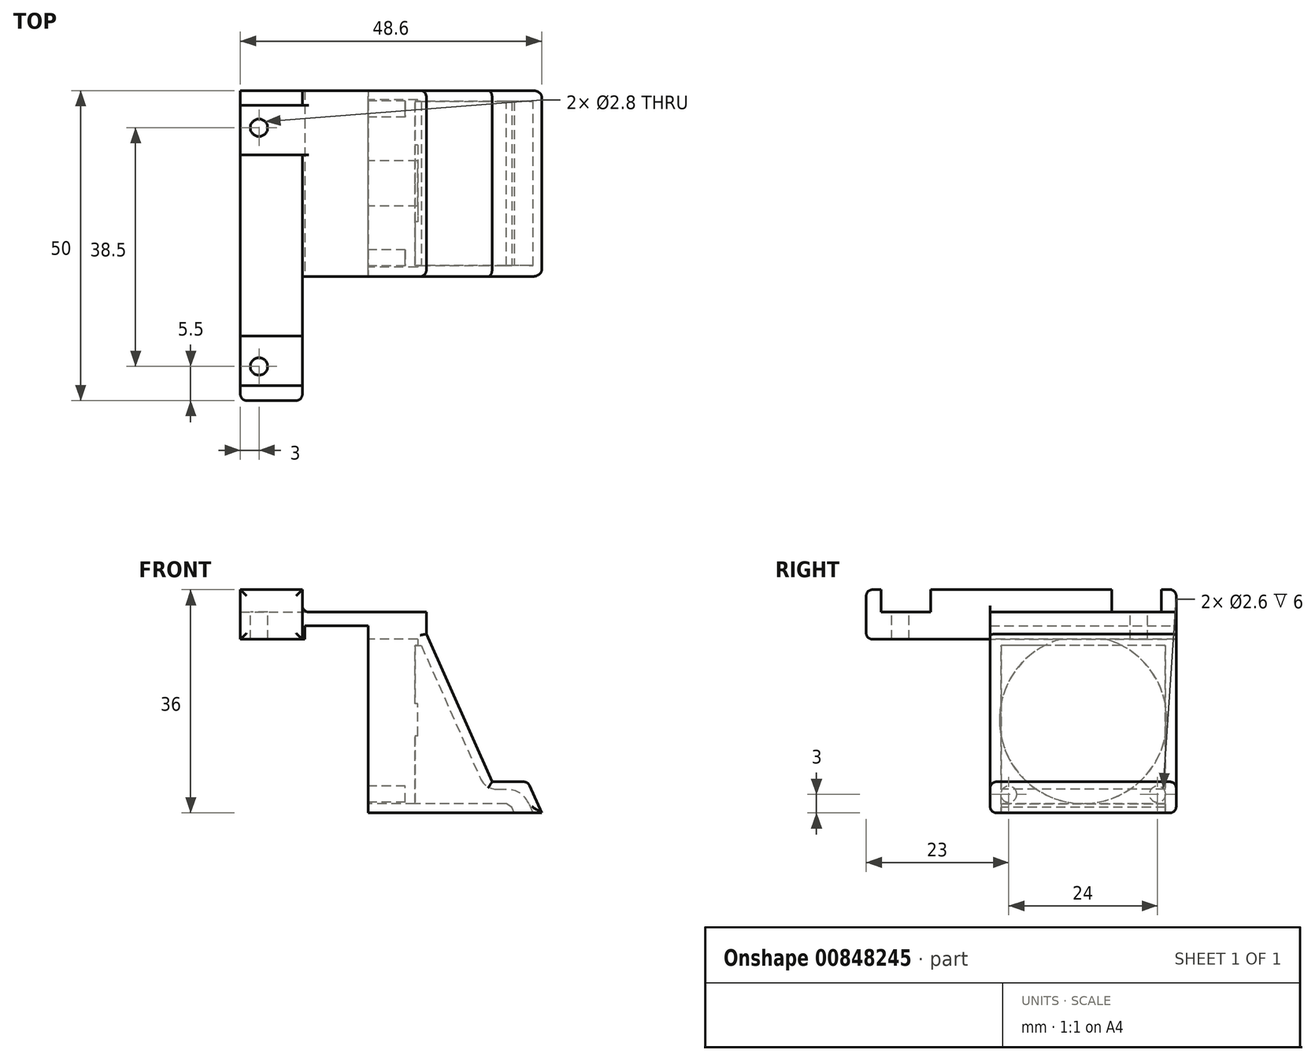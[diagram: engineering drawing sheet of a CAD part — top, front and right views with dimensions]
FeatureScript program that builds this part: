
annotation { "Feature Type Name" : "Feature", "Feature Type Description" : "" }
export const myFeature = defineFeature(function(context is Context, id is Id, definition is map)
    precondition{}
    {
        {
            var Q0;
            Q0=qCreatedBy(makeId("Front.planeOp"),FACE);
            var sketch = newSketch(context, id + "F0", { "sketchPlane" : qUnion([Q0])});
            skLineSegment(sketch, "E0", {"start": v(0, 0) * mm, "end": v(0, 32) * mm});
            skLineSegment(sketch, "E1", {"start": v(0, 32) * mm, "end": v(8, 32) * mm});
            skLineSegment(sketch, "E2", {"start": v(8, 32) * mm, "end": v(20, 5) * mm});
            skLineSegment(sketch, "E3", {"start": v(28, 0) * mm, "end": v(0, 0) * mm});
            skLineSegment(sketch, "E4", {"start": v(20, 5) * mm, "end": v(25.78, 5) * mm});
            skLineSegment(sketch, "E5", {"start": v(25.78, 5) * mm, "end": v(28, 0) * mm});
            skSolve(sketch);
        }
        {
            var Q0;
            Q0=makeQuery(id+"F0.imprint","IMPRINT",FACE,{"disambiguationData":[TD([[makeQuery(id+"F0.imprint","IMPRINT",EDGE,{"derivedFrom":sQuery(id+"F0.wireOp",EDGE,"E0")}),-1.0]])]});
            extrude(context, id + "F1", {"entities" : qUnion([Q0]), "depth" : 30 * mm, "offsetDistance" : 25 * mm});
        }
        {
            var Q0;
            Q0=makeQuery(id+"F1.opExtrude","SWEPT_FACE",FACE,{"disambiguationData":[OSD([sQuery(id+"F0.wireOp",EDGE,"E1")])]});
            var sketch = newSketch(context, id + "F2", { "sketchPlane" : qUnion([Q0])});
            skLineSegment(sketch, "E6.bottom", {"start": v(-20.6, -50) * mm, "end": v(-10.6, -50) * mm});
            skLineSegment(sketch, "E6.top", {"start": v(0, 0) * mm, "end": v(9.4, 0) * mm});
            skLineSegment(sketch, "E6.left", {"start": v(-20.6, -50) * mm, "end": v(-20.6, 0) * mm});
            skLineSegment(sketch, "E6.right", {"start": v(9.4, -30) * mm, "end": v(9.4, 0) * mm});
            skLineSegment(sketch, "E7", {"start": v(9.4, -30) * mm, "end": v(-10.6, -30) * mm});
            skLineSegment(sketch, "E8", {"start": v(-10.6, -30) * mm, "end": v(-10.6, -50) * mm});
            skLineSegment(sketch, "E9", {"start": v(9.4, 0) * mm, "end": v(0, 0) * mm});
            skLineSegment(sketch, "E10", {"start": v(-20.6, 0) * mm, "end": v(0, 0) * mm});
            skSolve(sketch);
        }
        {
            var Q0;
            Q0=qSketchRegion(id+"F2",true);
            extrude(context, id + "F3", {"entities" : qUnion([Q0]), "operationType" : NewBodyOperationType.ADD, "endBound" : BoundingType.SYMMETRIC, "oppositeDirection" : true, "depth" : 8 * mm, "offsetDistance" : 25 * mm});
        }
        {
            var Q0;
            Q0=qCreatedBy(makeId("Top.planeOp"),FACE);
            cPlane(context, id + "F4", {"entities" : qUnion([Q0]), "cplaneType" : CPlaneType.OFFSET, "offset" : 36 * mm, "width" : 150 * mm, "height" : 150 * mm});
        }
        {
            var Q0;
            Q0=qCreatedBy(id+"F4.planeOp",FACE);
            var sketch = newSketch(context, id + "F5", { "sketchPlane" : qUnion([Q0])});
            skLineSegment(sketch, "E11.bottom", {"start": v(-20.6, -39.6) * mm, "end": v(-10.6, -39.6) * mm});
            skLineSegment(sketch, "E11.top", {"start": v(-20.6, -47.6) * mm, "end": v(-10.6, -47.6) * mm});
            skLineSegment(sketch, "E11.left", {"start": v(-20.6, -39.6) * mm, "end": v(-20.6, -47.6) * mm});
            skLineSegment(sketch, "E11.right", {"start": v(-10.6, -39.6) * mm, "end": v(-10.6, -47.6) * mm});
            skLineSegment(sketch, "E12.bottom", {"start": v(-20.6, -2.4) * mm, "end": v(-10.6, -2.4) * mm});
            skLineSegment(sketch, "E12.top", {"start": v(-20.6, -10.4) * mm, "end": v(-10.6, -10.4) * mm});
            skLineSegment(sketch, "E12.left", {"start": v(-20.6, -2.4) * mm, "end": v(-20.6, -10.4) * mm});
            skLineSegment(sketch, "E13", {"start": v(-10.6, -30) * mm, "end": v(-10.6, -10.4) * mm});
            skLineSegment(sketch, "E14", {"start": v(-10.6, -30) * mm, "end": v(9.4, -30) * mm});
            skLineSegment(sketch, "E15", {"start": v(9.4, -30) * mm, "end": v(9.4, 0) * mm});
            skLineSegment(sketch, "E16", {"start": v(9.4, 0) * mm, "end": v(-10.6, 0) * mm});
            skLineSegment(sketch, "E17", {"start": v(-10.6, 0) * mm, "end": v(-10.6, -2.4) * mm});
            skPoint(sketch, "E18.orphan", {"position": v(-8.6, -2.4) * mm});
            skSolve(sketch);
        }
        {
            var Q0;
            Q0=makeQuery(id+"F5.imprint","IMPRINT",FACE,{"disambiguationData":[TD([[makeQuery(id+"F5.imprint","IMPRINT",EDGE,{"derivedFrom":sQuery(id+"F5.wireOp",EDGE,"E11.bottom")}),-1.0]])]});
            var Q1;
            Q1=makeQuery(id+"F5.imprint","IMPRINT",FACE,{"disambiguationData":[TD([[makeQuery(id+"F5.imprint","IMPRINT",EDGE,{"derivedFrom":sQuery(id+"F5.wireOp",EDGE,"E12.bottom")}),-1.0]])]});
            extrude(context, id + "F6", {"entities" : qUnion([Q0, Q1]), "operationType" : NewBodyOperationType.REMOVE, "oppositeDirection" : true, "depth" : 3.6 * mm, "offsetDistance" : 25 * mm});
        }
        {
            var Q0;
            Q0=qCreatedBy(makeId("Front.planeOp"),FACE);
            cPlane(context, id + "F7", {"entities" : qUnion([Q0]), "cplaneType" : CPlaneType.OFFSET, "offset" : 28.25 * mm, "width" : 150 * mm, "height" : 150 * mm});
        }
        {
            var Q0;
            Q0=qCreatedBy(id+"F7.planeOp",FACE);
            var sketch = newSketch(context, id + "F8", { "sketchPlane" : qUnion([Q0])});
            skLineSegment(sketch, "E19", {"start": v(8.58, 27) * mm, "end": v(18.9, 3.8) * mm});
            skLineSegment(sketch, "E20", {"start": v(27.5, -2) * mm, "end": v(24.5, -2) * mm});
            skLineSegment(sketch, "E21", {"start": v(24.5, -2) * mm, "end": v(22.94, 1.5) * mm});
            skLineSegment(sketch, "E22", {"start": v(22.94, 1.5) * mm, "end": v(7.58, 1.5) * mm});
            skLineSegment(sketch, "E23", {"start": v(7.58, 1.5) * mm, "end": v(7.58, 27) * mm});
            skLineSegment(sketch, "E24", {"start": v(7.58, 27) * mm, "end": v(8.58, 27) * mm});
            skLineSegment(sketch, "E25", {"start": v(18.9, 3.8) * mm, "end": v(24.92, 3.8) * mm});
            skLineSegment(sketch, "E26", {"start": v(24.92, 3.8) * mm, "end": v(27.5, -2) * mm});
            skSolve(sketch);
        }
        {
            var Q0;
            Q0=qSketchRegion(id+"F8",true);
            extrude(context, id + "F9", {"entities" : qUnion([Q0]), "operationType" : NewBodyOperationType.REMOVE, "oppositeDirection" : true, "depth" : 26.5 * mm, "offsetDistance" : 25 * mm});
        }
        {
            var Q0;
            Q0=qCreatedBy(makeId("Right.planeOp"),FACE);
            var sketch = newSketch(context, id + "F10", { "sketchPlane" : qUnion([Q0])});
            skArc(sketch, "E27", {"start": v(-18.64, 28) * mm, "mid": v(-15, 1.5) * mm, "end": v(-11.36, 28) * mm});
            skLineSegment(sketch, "E28", {"start": v(-18.64, 28) * mm, "end": v(-11.36, 28) * mm});
            skSolve(sketch);
        }
        {
            var Q0;
            Q0=makeQuery(id+"F10.imprint","IMPRINT",FACE,{"disambiguationData":[TD([[makeQuery(id+"F10.imprint","IMPRINT",EDGE,{"derivedFrom":sQuery(id+"F10.wireOp",EDGE,"E27")}),1.0]])]});
            extrude(context, id + "F11", {"entities" : qUnion([Q0]), "operationType" : NewBodyOperationType.REMOVE, "depth" : 8 * mm, "offsetDistance" : 25 * mm});
        }
        {
            var Q0;
            Q0=qCreatedBy(makeId("Right.planeOp"),FACE);
            var sketch = newSketch(context, id + "F12", { "sketchPlane" : qUnion([Q0])});
            skCircle(sketch, "E29", {"center": v(-27, 3) * mm, "radius": 1.3 * mm});
            skCircle(sketch, "E30", {"center": v(-3, 3) * mm, "radius": 1.3 * mm});
            skSolve(sketch);
        }
        {
            var Q0;
            Q0=qSketchRegion(id+"F12",true);
            extrude(context, id + "F13", {"entities" : qUnion([Q0]), "operationType" : NewBodyOperationType.REMOVE, "depth" : 6 * mm, "offsetDistance" : 25 * mm});
        }
        {
            var Q0;
            Q0=makeQuery(id+"F6.boolean.opBoolean","COPY",FACE,{"derivedFrom":makeQuery(id+"F6.opExtrude","CAP_FACE",FACE,{"disambiguationData":[OSD([sQuery(id+"F5.wireOp",EDGE,"E11.bottom"),sQuery(id+"F5.wireOp",EDGE,"E11.top"),sQuery(id+"F5.wireOp",EDGE,"E11.left"),sQuery(id+"F5.wireOp",EDGE,"E11.right")])],"isStart":false})});
            var sketch = newSketch(context, id + "F14", { "sketchPlane" : qUnion([Q0])});
            skCircle(sketch, "E31", {"center": v(-17.6, -44.5) * mm, "radius": 1.4 * mm});
            skSolve(sketch);
        }
        {
            var Q0;
            Q0=makeQuery(id+"F6.boolean.opBoolean","COPY",FACE,{"derivedFrom":makeQuery(id+"F6.opExtrude","CAP_FACE",FACE,{"disambiguationData":[OSD([sQuery(id+"F5.wireOp",EDGE,"E12.bottom"),sQuery(id+"F5.wireOp",EDGE,"E12.top"),sQuery(id+"F5.wireOp",EDGE,"E12.left"),sQuery(id+"F5.wireOp",EDGE,"E12.right")])],"isStart":false})});
            var sketch = newSketch(context, id + "F15", { "sketchPlane" : qUnion([Q0])});
            skCircle(sketch, "E32", {"center": v(-17.6, -6) * mm, "radius": 1.4 * mm});
            skSolve(sketch);
        }
        {
            var Q0;
            Q0=qSketchRegion(id+"F14",true);
            extrude(context, id + "F16", {"entities" : qUnion([Q0]), "operationType" : NewBodyOperationType.REMOVE, "oppositeDirection" : true, "depth" : 5 * mm, "offsetDistance" : 25 * mm});
        }
        {
            var Q0;
            Q0=qSketchRegion(id+"F15",true);
            extrude(context, id + "F17", {"entities" : qUnion([Q0]), "operationType" : NewBodyOperationType.REMOVE, "oppositeDirection" : true, "depth" : 5 * mm, "offsetDistance" : 25 * mm});
        }
        {
            var Q0;
            Q0=makeQuery(id+"F9.boolean.opBoolean","COPY",EDGE,{"derivedFrom":makeQuery(id+"F9.opExtrude","SWEPT_EDGE",EDGE,{"disambiguationData":[OSD([sQuery(id+"F8.wireOp",EDGE,"E19"),sQuery(id+"F8.wireOp",EDGE,"E25")])]})});
            fillet(context, id + "F18", {"entities" : qUnion([Q0]), "radius" : 3 * mm, "tangentPropagation" : true, "allowEdgeOverflow" : false});
        }
        {
            var Q0;
            Q0=makeQuery(id+"F9.boolean.opBoolean","COPY",EDGE,{"derivedFrom":makeQuery(id+"F9.opExtrude","SWEPT_EDGE",EDGE,{"disambiguationData":[OSD([sQuery(id+"F8.wireOp",EDGE,"E25"),sQuery(id+"F8.wireOp",EDGE,"E26")])]})});
            fillet(context, id + "F19", {"entities" : qUnion([Q0]), "radius" : 4 * mm, "tangentPropagation" : true, "allowEdgeOverflow" : false});
        }
        {
            var Q0;
            Q0=makeQuery(id+"F9.boolean.opBoolean","COPY",EDGE,{"derivedFrom":makeQuery(id+"F9.opExtrude","SWEPT_EDGE",EDGE,{"disambiguationData":[OSD([sQuery(id+"F8.wireOp",EDGE,"E21"),sQuery(id+"F8.wireOp",EDGE,"E22")])]})});
            chamfer(context, id + "F20", {"entities" : qUnion([Q0]), "width" : 1 * mm, "tangentPropagation" : true});
        }
        {
            var Q0;
            Q0=makeQuery(id+"F1.opExtrude","CAP_EDGE",EDGE,{"disambiguationData":[OSD([sQuery(id+"F0.wireOp",EDGE,"E3")])],"isStart":false});
            var Q1;
            Q1=makeQuery(id+"F1.opExtrude","CAP_EDGE",EDGE,{"disambiguationData":[OSD([sQuery(id+"F0.wireOp",EDGE,"E2")])],"isStart":false});
            var Q2;
            Q2=makeQuery(id+"F1.opExtrude","CAP_EDGE",EDGE,{"disambiguationData":[OSD([sQuery(id+"F0.wireOp",EDGE,"E4")])],"isStart":false});
            var Q3;
            Q3=makeQuery(id+"F1.opExtrude","CAP_EDGE",EDGE,{"disambiguationData":[OSD([sQuery(id+"F0.wireOp",EDGE,"E5")])],"isStart":false});
            var Q4;
            Q4=makeQuery(id+"F1.opExtrude","CAP_EDGE",EDGE,{"disambiguationData":[OSD([sQuery(id+"F0.wireOp",EDGE,"E2")])],"isStart":true});
            var Q5;
            Q5=makeQuery(id+"F1.opExtrude","CAP_EDGE",EDGE,{"disambiguationData":[OSD([sQuery(id+"F0.wireOp",EDGE,"E4")])],"isStart":true});
            var Q6;
            Q6=makeQuery(id+"F1.opExtrude","CAP_EDGE",EDGE,{"disambiguationData":[OSD([sQuery(id+"F0.wireOp",EDGE,"E5")])],"isStart":true});
            var Q7;
            Q7=makeQuery(id+"F1.opExtrude","CAP_EDGE",EDGE,{"disambiguationData":[OSD([sQuery(id+"F0.wireOp",EDGE,"E3")])],"isStart":true});
            var Q8;
            Q8=makeQuery(id+"F1.opExtrude","SWEPT_EDGE",EDGE,{"disambiguationData":[OSD([sQuery(id+"F0.wireOp",EDGE,"E4"),sQuery(id+"F0.wireOp",EDGE,"E5")])]});
            fillet(context, id + "F21", {"entities" : qUnion([Q0, Q1, Q2, Q3, Q4, Q5, Q6, Q7, Q8]), "radius" : 1 * mm, "tangentPropagation" : true, "allowEdgeOverflow" : false});
        }
        {
            var Q0;
            Q0=qCreatedBy(makeId("Front.planeOp"),FACE);
            var sketch = newSketch(context, id + "F22", { "sketchPlane" : qUnion([Q0])});
            skLineSegment(sketch, "E33.bottom", {"start": v(0, 0) * mm, "end": v(-10.2, 0) * mm});
            skLineSegment(sketch, "E33.top", {"start": v(0, 30.2) * mm, "end": v(-10.2, 30.2) * mm});
            skLineSegment(sketch, "E33.left", {"start": v(0, 0) * mm, "end": v(0, 30.2) * mm});
            skLineSegment(sketch, "E33.right", {"start": v(-10.2, 0) * mm, "end": v(-10.2, 30.2) * mm});
            skSolve(sketch);
        }
        {
            var Q0;
            Q0=makeQuery(id+"F22.imprint","IMPRINT",FACE,{"disambiguationData":[TD([[makeQuery(id+"F22.imprint","IMPRINT",EDGE,{"derivedFrom":sQuery(id+"F22.wireOp",EDGE,"E33.bottom")}),-1.0]])]});
            extrude(context, id + "F23", {"entities" : qUnion([Q0]), "operationType" : NewBodyOperationType.REMOVE, "depth" : 30 * mm, "offsetDistance" : 25 * mm});
        }
        {
            var Q0;
            Q0=makeQuery(id+"F6.boolean.opBoolean","COPY",EDGE,{"derivedFrom":makeQuery(id+"F6.opExtrude","CAP_EDGE",EDGE,{"disambiguationData":[OSD([sQuery(id+"F5.wireOp",EDGE,"E15")])],"isStart":false})});
            var Q1;
            Q1=makeQuery(id+"F6.boolean.opBoolean","COPY",EDGE,{"derivedFrom":makeQuery(id+"F6.opExtrude","CAP_EDGE",EDGE,{"disambiguationData":[OSD([sQuery(id+"F5.wireOp",EDGE,"E16")])],"isStart":false})});
            var Q2;
            Q2=makeQuery(id+"F6.boolean.opBoolean","COPY",EDGE,{"derivedFrom":makeQuery(id+"F6.opExtrude","CAP_EDGE",EDGE,{"disambiguationData":[OSD([sQuery(id+"F5.wireOp",EDGE,"E14")])],"isStart":false})});
            var Q3;
            Q3=makeQuery(id+"F6.boolean.opBoolean","COPY",EDGE,{"derivedFrom":makeQuery(id+"F6.opExtrude","CAP_EDGE",EDGE,{"disambiguationData":[OSD([sQuery(id+"F5.wireOp",EDGE,"E13")])],"isStart":false})});
            var Q4;
            Q4=makeQuery(id+"F6.boolean.opBoolean","COPY",EDGE,{"derivedFrom":makeQuery(id+"F6.opExtrude","CAP_EDGE",EDGE,{"disambiguationData":[OSD([sQuery(id+"F5.wireOp",EDGE,"E17")])],"isStart":false})});
            var Q5;
            Q5=makeQuery(id+"F3.opExtrude","CAP_EDGE",EDGE,{"disambiguationData":[OSD([sQuery(id+"F2.wireOp",EDGE,"E9"),sQuery(id+"F2.wireOp",EDGE,"E10")])],"isStart":true});
            var Q6;
            Q6=makeQuery(id+"F3.opExtrude","SWEPT_EDGE",EDGE,{"disambiguationData":[OSD([sQuery(id+"F2.wireOp",EDGE,"E6.bottom"),sQuery(id+"F2.wireOp",EDGE,"E8")])]});
            var Q7;
            Q7=makeQuery(id+"F3.opExtrude","CAP_EDGE",EDGE,{"disambiguationData":[OSD([sQuery(id+"F2.wireOp",EDGE,"E6.bottom")])],"isStart":true});
            var Q8;
            Q8=makeQuery(id+"F3.opExtrude","SWEPT_EDGE",EDGE,{"disambiguationData":[OSD([sQuery(id+"F2.wireOp",EDGE,"E6.bottom"),sQuery(id+"F2.wireOp",EDGE,"E6.left")])]});
            var Q9;
            Q9=makeQuery(id+"F3.opExtrude","CAP_EDGE",EDGE,{"disambiguationData":[OSD([sQuery(id+"F2.wireOp",EDGE,"E6.bottom")])],"isStart":false});
            var Q10;
            Q10=makeQuery(id+"F3.opExtrude","SWEPT_EDGE",EDGE,{"disambiguationData":[OSD([sQuery(id+"F2.wireOp",EDGE,"E6.right"),sQuery(id+"F2.wireOp",EDGE,"E7")])]});
            var Q11;
            Q11=makeQuery(id+"F3.opExtrude","SWEPT_EDGE",EDGE,{"disambiguationData":[OSD([sQuery(id+"F2.wireOp",EDGE,"E6.right"),sQuery(id+"F2.wireOp",EDGE,"E9")])]});
            fillet(context, id + "F24", {"entities" : qUnion([Q0, Q1, Q2, Q3, Q4, Q5, Q6, Q7, Q8, Q9, Q10, Q11]), "radius" : 1 * mm, "tangentPropagation" : true, "allowEdgeOverflow" : false});
        }
    });
